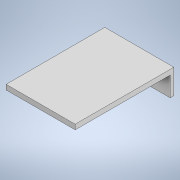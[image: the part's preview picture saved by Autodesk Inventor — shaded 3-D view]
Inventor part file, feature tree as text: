
AUTODESK INVENTOR PART (.ipt)
format: ipt  version: 2021.2 (Build 252289000, 289)  size: 160,256 bytes
history: native  units: in
note: dims shown in document units (in); Inventor stores cm internally (conversion verified against a paired STEP export)
features: sketch x6, extrude x5, other x4, hole x1
ambient origin geometry x8: Origin, YZ Plane, XZ Plane, XY Plane, X Axis, Y Axis, Z Axis, Center Point
bodies: Solid1 (feature_tree)
feature tree (16):
  other  "Annotations"
  extrude  "Extrusion1"  Depth=3.5in
  extrude  "Extrusion5"  Depth=0.1875in
  extrude  "Extrusion2"  Depth=0.1875in
  extrude  "Extrusion3"  Depth=0.1875in
  extrude  "Extrusion4"  Depth=0.125in
  hole  "Hole1"  [1 undecoded]
  sketch  "Sketch2"  dims[d0=5.0in d1=3.5in]
  sketch  "Sketch4"  dims[d2=0.25in d3=0.0in d4=0.1875in]
  sketch  "Sketch5"  dims[d5=3.0in d6=0.0in d7=0.1875in]
  sketch  "Sketch6"  dims[d8=0.1875in d9=3.0in]
  sketch  "Sketch7"  dims[d10=0.0in d11=0.125in]
  sketch  "Sketch9"  dims[d12=0.125in d13=0.125in d14=0.6875in d15=0.6875in d16=0.6875in d17=0.6875in d18=0.3438in d19=2.0in d20=0.0in d21=0.15in d22=0.75in d23=0.279in d24=0.25in d25=0.5635in d26=1.0in d27=0.8108in d35=0.1875in d36=1.0in d37=0.0in d28=0.0718in d29=0.1553in d30=0.6875in d31=0.2658in d32=3.25in d33=0.2063in d34=2.0in]
  other  "Linear Dimension 1"
  other  "Linear Dimension 2"
  other  "Linear Dimension 3"
note: 1 required parameter value undecoded (feature->parameter linkage not recoverable at this tier; creation-order binding heuristic only, values carry confidence <= 0.55)
